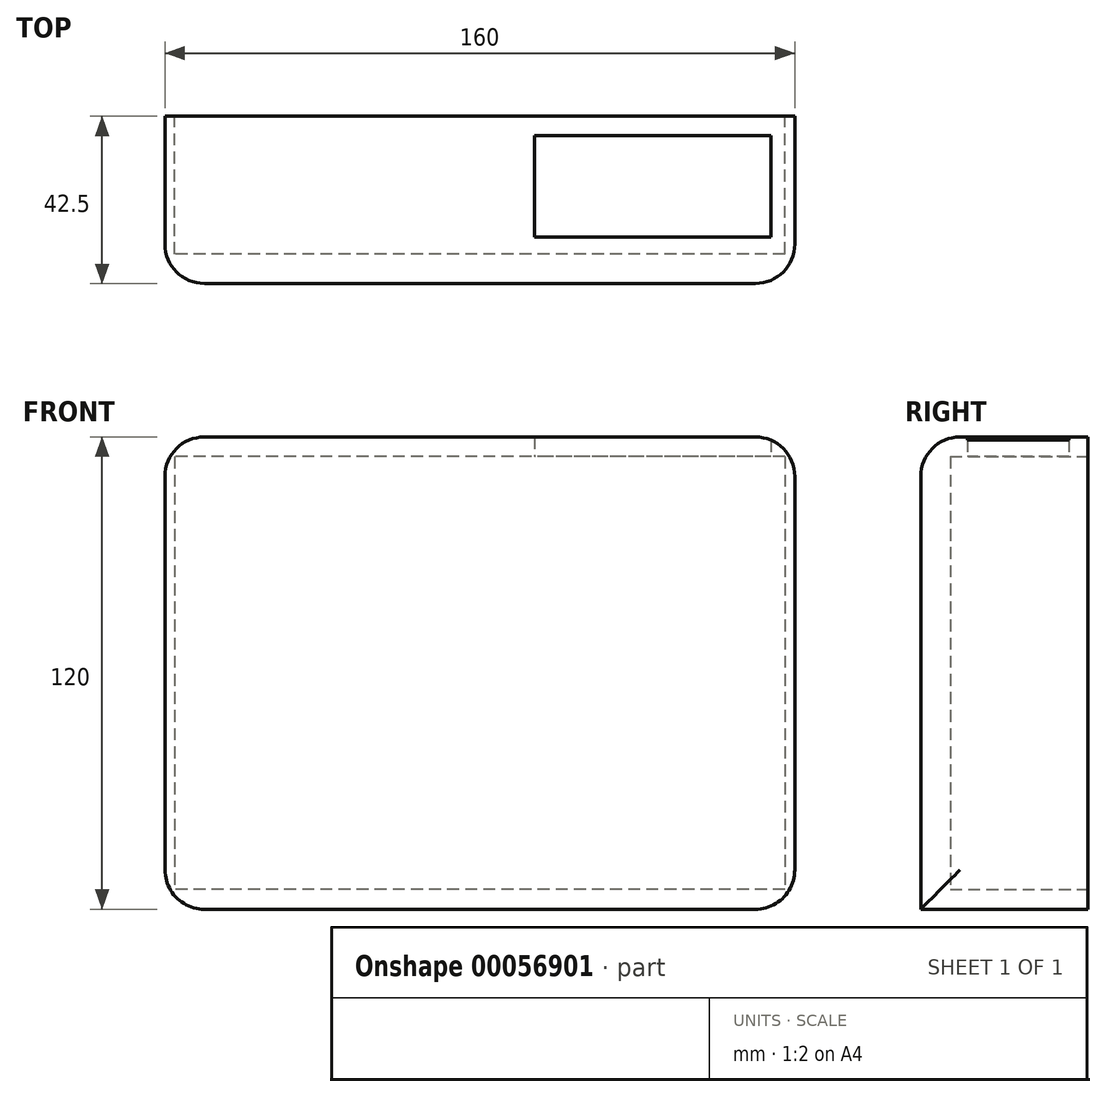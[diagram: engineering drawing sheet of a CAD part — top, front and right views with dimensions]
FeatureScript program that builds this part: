
annotation { "Feature Type Name" : "Feature", "Feature Type Description" : "" }
export const myFeature = defineFeature(function(context is Context, id is Id, definition is map)
    precondition{}
    {
        {
            var Q0;
            Q0=qCreatedBy(makeId("Front.planeOp"),FACE);
            var sketch = newSketch(context, id + "F0", { "sketchPlane" : qUnion([Q0])});
            skLineSegment(sketch, "E0.bottom", {"start": v(-72.42, 62.32) * mm, "end": v(87.58, 62.32) * mm});
            skLineSegment(sketch, "E0.top", {"start": v(-72.42, -57.68) * mm, "end": v(87.58, -57.68) * mm});
            skLineSegment(sketch, "E0.left", {"start": v(-72.42, 62.32) * mm, "end": v(-72.42, -57.68) * mm});
            skLineSegment(sketch, "E0.right", {"start": v(87.58, 62.32) * mm, "end": v(87.58, -57.68) * mm});
            skSolve(sketch);
        }
        {
            var Q0;
            Q0 = qSketchRegion(id + "F0", true);
            extrude(context, id + "F1", {"entities" : qUnion([Q0]), "depth" : 42.5 * mm});
        }
        {
            var Q0;
            Q0=makeQuery(id+"F1.opExtrude","SWEPT_EDGE",EDGE,{"disambiguationData":[OSD([sQuery(id+"F0.wireOp",EDGE,"E0.bottom"),sQuery(id+"F0.wireOp",EDGE,"E0.right")])]});
            var Q1;
            Q1=makeQuery(id+"F1.opExtrude","SWEPT_EDGE",EDGE,{"disambiguationData":[OSD([sQuery(id+"F0.wireOp",EDGE,"E0.bottom"),sQuery(id+"F0.wireOp",EDGE,"E0.left")])]});
            var Q2;
            Q2=makeQuery(id+"F1.opExtrude","SWEPT_EDGE",EDGE,{"disambiguationData":[OSD([sQuery(id+"F0.wireOp",EDGE,"E0.top"),sQuery(id+"F0.wireOp",EDGE,"E0.right")])]});
            var Q3;
            Q3=makeQuery(id+"F1.opExtrude","SWEPT_EDGE",EDGE,{"disambiguationData":[OSD([sQuery(id+"F0.wireOp",EDGE,"E0.top"),sQuery(id+"F0.wireOp",EDGE,"E0.left")])]});
            var Q4;
            Q4=makeQuery(id+"F1.opExtrude","CAP_EDGE",EDGE,{"disambiguationData":[OSD([sQuery(id+"F0.wireOp",EDGE,"E0.left")])],"isStart":false});
            var Q5;
            Q5=makeQuery(id+"F1.opExtrude","CAP_EDGE",EDGE,{"disambiguationData":[OSD([sQuery(id+"F0.wireOp",EDGE,"E0.right")])],"isStart":false});
            var Q6;
            Q6=makeQuery(id+"F1.opExtrude","CAP_EDGE",EDGE,{"disambiguationData":[OSD([sQuery(id+"F0.wireOp",EDGE,"E0.bottom")])],"isStart":false});
            fillet(context, id + "F2", {"entities" : qUnion([Q0, Q1, Q2, Q3, Q4, Q5, Q6]), "radius" : 10 * mm, "tangentPropagation" : true, "allowEdgeOverflow" : false});
        }
        {
            var Q0;
            Q0=qCreatedBy(makeId("Front.planeOp"),FACE);
            var sketch = newSketch(context, id + "F3", { "sketchPlane" : qUnion([Q0])});
            skLineSegment(sketch, "E1.bottom", {"start": v(85.08, 57.32) * mm, "end": v(-69.92, 57.32) * mm});
            skLineSegment(sketch, "E1.top", {"start": v(85.08, -52.68) * mm, "end": v(-69.92, -52.68) * mm});
            skLineSegment(sketch, "E1.left", {"start": v(85.08, 57.32) * mm, "end": v(85.08, -52.68) * mm});
            skLineSegment(sketch, "E1.right", {"start": v(-69.92, 57.32) * mm, "end": v(-69.92, -52.68) * mm});
            skSolve(sketch);
        }
        {
            var Q0;
            Q0 = qSketchRegion(id + "F3", true);
            extrude(context, id + "F4", {"entities" : qUnion([Q0]), "operationType" : NewBodyOperationType.REMOVE, "depth" : 35 * mm});
        }
        {
            var Q0;
            Q0=makeQuery(id+"F4.boolean.opBoolean","COPY",FACE,{"derivedFrom":makeQuery(id+"F4.opExtrude","SWEPT_FACE",FACE,{"disambiguationData":[OSD([sQuery(id+"F3.wireOp",EDGE,"E1.bottom")])]})});
            var sketch = newSketch(context, id + "F5", { "sketchPlane" : qUnion([Q0])});
            skLineSegment(sketch, "E2.bottom", {"start": v(81.54, 4.91) * mm, "end": v(21.45, 4.91) * mm});
            skLineSegment(sketch, "E2.top", {"start": v(81.54, 30.67) * mm, "end": v(21.45, 30.67) * mm});
            skLineSegment(sketch, "E2.left", {"start": v(81.54, 4.91) * mm, "end": v(81.54, 30.67) * mm});
            skLineSegment(sketch, "E2.right", {"start": v(21.45, 4.91) * mm, "end": v(21.45, 30.67) * mm});
            skSolve(sketch);
        }
        {
            var Q0;
            Q0=makeQuery(id+"F5.imprint","IMPRINT",FACE,{"disambiguationData":[TD([[makeQuery(id+"F5.imprint","IMPRINT",EDGE,{"derivedFrom":sQuery(id+"F5.wireOp",EDGE,"E2.bottom")}),-1.0]])]});
            extrude(context, id + "F6", {"entities" : qUnion([Q0]), "operationType" : NewBodyOperationType.REMOVE, "endBound" : BoundingType.THROUGH_ALL, "oppositeDirection" : true, "depth" : 25 * mm});
        }
    });
